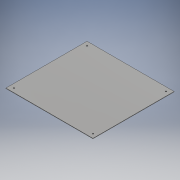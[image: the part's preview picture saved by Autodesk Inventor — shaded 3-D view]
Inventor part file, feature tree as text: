
AUTODESK INVENTOR PART (.ipt)
format: ipt  version: 2018 (Build 220112000, 112)  size: 122,368 bytes
history: native  units: mm
features: sketch x5, hole x4, extrude x1
ambient origin geometry x8: Origin, YZ Plane, XZ Plane, XY Plane, X Axis, Y Axis, Z Axis, Center Point
bodies: Solid1 (feature_tree)
feature tree (10):
  extrude  "Extrusion1"  Depth=411.0mm
  hole  "Hole1"  [1 undecoded]
  hole  "Hole2"  [1 undecoded]
  hole  "Hole3"  [1 undecoded]
  hole  "Hole4"  [1 undecoded]
  sketch  "Sketch1"  dims[d0=383.0mm d1=411.0mm]
  sketch  "Sketch2"  dims[d2=2.0mm d3=0.0mm d4=18.82mm]
  sketch  "Sketch3"  dims[d5=19.0mm d6=6.0mm]
  sketch  "Sketch4"  dims[d7=6.0mm d8=6.0mm d9=4.0mm d10=2.0mm d11=90.0deg d12=8.0mm d13=20.594885mm d14=18.82mm]
  sketch  "Sketch5"  dims[d15=19.0mm d16=6.0mm d17=6.0mm d18=6.0mm d19=4.0mm d20=2.0mm d21=90.0deg d22=8.0mm d23=20.594885mm d24=18.82mm d25=19.0mm d26=6.0mm d27=6.0mm d28=6.0mm d29=4.0mm d30=2.0mm d31=90.0deg d32=8.0mm d33=20.594885mm d34=18.82mm d35=19.0mm d36=6.0mm d37=6.0mm d38=6.0mm d39=4.0mm d40=2.0mm d41=90.0deg d42=8.0mm d43=20.594885mm]
note: 4 required parameter values undecoded (feature->parameter linkage not recoverable at this tier; creation-order binding heuristic only, values carry confidence <= 0.55)
